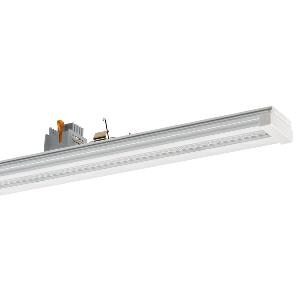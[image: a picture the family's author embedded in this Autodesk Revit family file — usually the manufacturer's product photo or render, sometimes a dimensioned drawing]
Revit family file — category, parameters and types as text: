
# Revit family: conveo_-_cvg_8000_840_w-l_da_7_226848279-00804966_ed61
name_source: partatom
category: Lighting Fixtures
units: mm (PartAtom-declared; Revit-internal decimal feet)

## family parameters
Cut with Voids When Loaded = No
Host = Face
Light Source = No
Part Type = Normal
Room Calculation Point = No
Round Connector Dimension = Use Diameter
Shared = No

## types (1)
- CONVEO - CVG 8000/840/W-L/DA/7 (1 x LED, 8100 lm, 4000K)
    Apparent Load = 47 VA
    Approval mark = CE
    CIE Flux Codes = 85 97 99 100 100
    Color Rendering = 80-89
    Color Temperature = 4000K
    Control Gear = Electronic ballast
    Default Elevation = 1800 mm
    Description = CVG 8000/840/W-L/DA/7|Continuous-row system|light source: LED|work equipment: Adjustable electronic ballast, digital DALI|connected load: 220-240 V, 50-60 Hz|Power consumption: approx. 47 W|luminous flux: 8100 lm|luminous efficacy: 172 lm/W|colour temperature: Cold white, ca. 4000 K|color rendering index (CRI): >= 80|chromaticity tolerance:  3 SDCM|System of protection: IP 54|class of protection: I|technology: Continuously dimmable|luminaire body|material: Aluminium|surface: Powder coatet|colour: White|lamp cover: Acrylic (PMMA), Satine|weight (net): approx. 1.9 kg|Fastening: Available separately|maximum ambient temperature: 42 ░C|glare control: Lens optics|Approval mark: VDE - ENEC|
    Frequency = 50 Hz
    Height = 70 mm
    Lamp = 1 x LED
    Lamp Light Flux = 8100 lm
    Lamp count = 1
    Length = 1500 mm
    Luminous efficacy = 172 lm/W
    Manufacturer = Waldmann
    ModVariant = No
    Model = 226848279-00804966
    Mounting Place = Ceiling
    Mounting Type = Pendant
    Number of Poles = 1
    OnlyDefault = Yes
    Power Factor = 1
    Product Name = CONVEO - CVG 8000/840/W-L/DA/7
    Product group = Continuous-row system (industry)
    ProductGroupID = 301
    Protection Class = Protection class I
    Protection Degree = IP 54
    RLX_Detail_Level = 1
    RlxData = <blob elided: 100025 chars, md5=d496cbee>
    Socket = socket
    Standby Power = 0 W
    System Light Flux = 8100 lm
    System Power = 47 W
    Type Comments = Product without accessories
    Type Image = 226848259-00804964_1l7.jpg
    URL = http://relux.com
    VarID = ---
    Voltage = 230 V
    Voltage Range = 220-240 V
    Weight = 0.00 kg
    Width = 64 mm

## geometry (parser evidence)
native form markers: Blend x4, Sweep x10
no freeform markers — native parametric forms only
